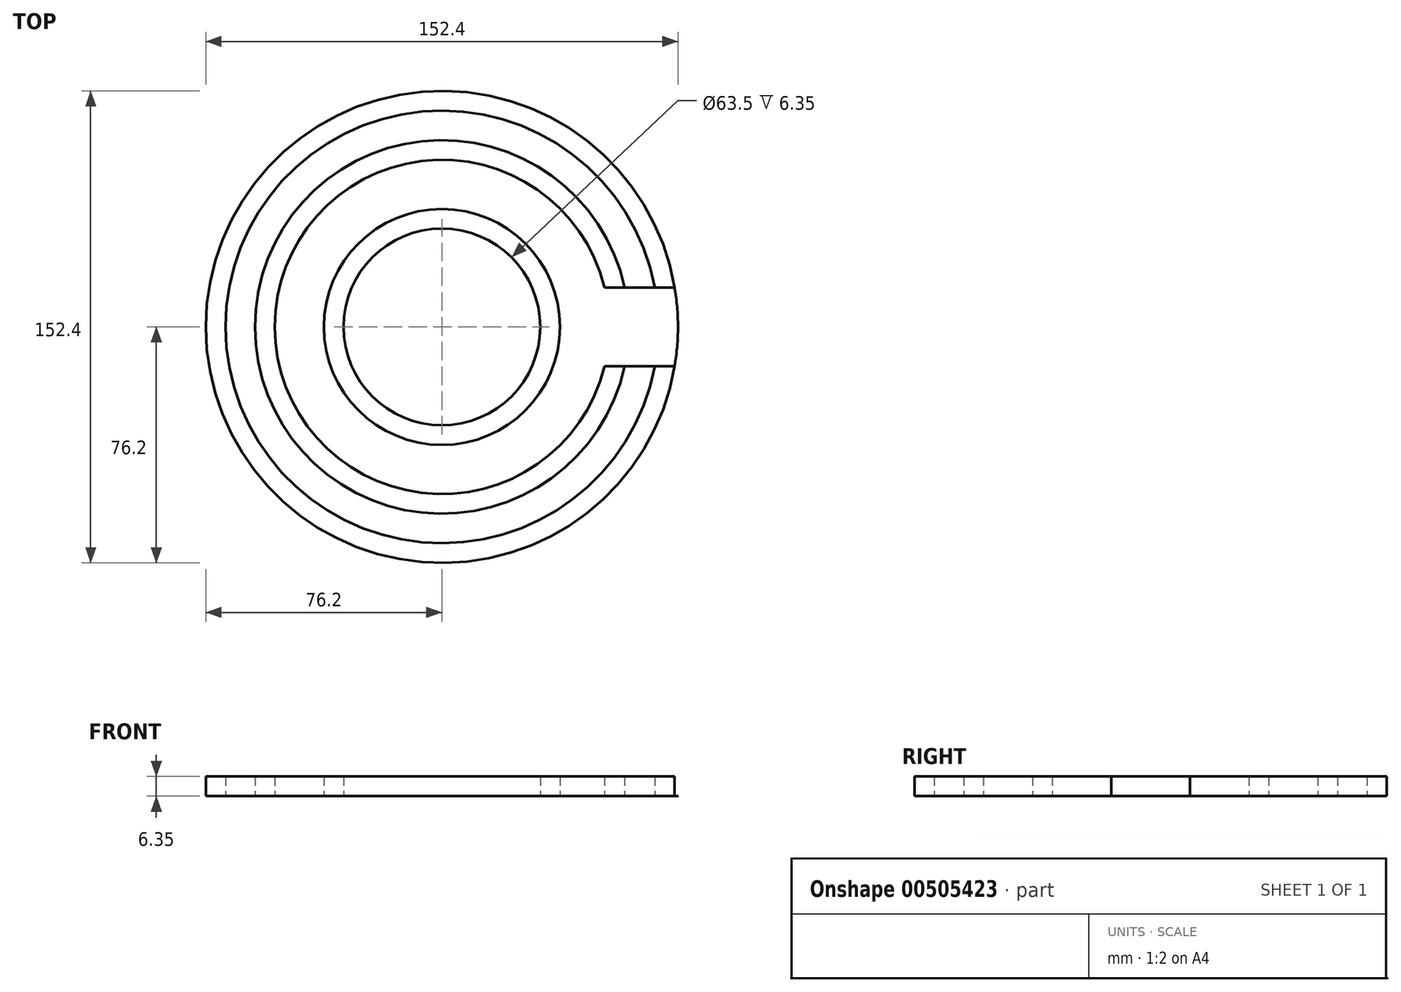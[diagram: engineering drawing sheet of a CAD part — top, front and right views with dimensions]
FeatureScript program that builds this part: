
annotation { "Feature Type Name" : "Feature", "Feature Type Description" : "" }
export const myFeature = defineFeature(function(context is Context, id is Id, definition is map)
    precondition{}
    {
        {
            var Q0;
            Q0=qCreatedBy(makeId("Top.planeOp"),FACE);
            var sketch = newSketch(context, id + "F0", { "sketchPlane" : qUnion([Q0])});
            skCircle(sketch, "E0", {"center": v(0, 0) * mm, "radius": 76.2 * mm});
            skCircle(sketch, "E1", {"center": v(0, 0) * mm, "radius": 69.85 * mm});
            skCircle(sketch, "E2", {"center": v(0, 0) * mm, "radius": 60.33 * mm});
            skCircle(sketch, "E3", {"center": v(0, 0) * mm, "radius": 53.98 * mm});
            skCircle(sketch, "E4", {"center": v(0, 0) * mm, "radius": 38.1 * mm});
            skCircle(sketch, "E5", {"center": v(0, 0) * mm, "radius": 31.75 * mm});
            skLineSegment(sketch, "E6", {"start": v(48.66, 12.7) * mm, "end": v(80.06, 12.7) * mm});
            skLineSegment(sketch, "E7", {"start": v(48.66, -12.7) * mm, "end": v(80.06, -12.7) * mm});
            skSolve(sketch);
        }
        {
            var Q0;
            {var subQ0=sQuery(id+"F0.wireOp",EDGE,"E6");var subQ1=sQuery(id+"F0.wireOp",EDGE,"E1");var subQ2=makeQuery(id+"F0.imprint","INTERSECT",VERTEX,{"derivedFrom":[subQ1,subQ0]});Q0=makeQuery(id+"F0.imprint","IMPRINT",FACE,{"disambiguationData":[TD([[makeQuery(id+"F0.imprint","IMPRINT",EDGE,{"disambiguationData":[TD([[subQ2,-1.0]])],"derivedFrom":subQ1}),1.0]])]});}
            var Q1;
            Q1=makeQuery(id+"F0.imprint","IMPRINT",FACE,{"disambiguationData":[TD([[makeQuery(id+"F0.imprint","IMPRINT",EDGE,{"derivedFrom":sQuery(id+"F0.wireOp",EDGE,"E5")}),1.0]])]});
            extrude(context, id + "F1", {"entities" : qUnion([Q0, Q1]), "depth" : 6.35 * mm});
        }
        {
            var Q0;
            Q0=qCreatedBy(makeId("Top.planeOp"),FACE);
            var sketch = newSketch(context, id + "F2", { "sketchPlane" : qUnion([Q0])});
            skCircle(sketch, "E8", {"center": v(0, 0) * mm, "radius": 76.2 * mm});
            skCircle(sketch, "E9", {"center": v(0, 0) * mm, "radius": 69.85 * mm});
            skCircle(sketch, "E10", {"center": v(0, 0) * mm, "radius": 60.33 * mm});
            skCircle(sketch, "E11", {"center": v(0, 0) * mm, "radius": 53.98 * mm});
            skCircle(sketch, "E12", {"center": v(0, 0) * mm, "radius": 38.1 * mm});
            skCircle(sketch, "E13", {"center": v(0, 0) * mm, "radius": 31.75 * mm});
            skLineSegment(sketch, "E14", {"start": v(48.66, 12.7) * mm, "end": v(80.06, 12.7) * mm});
            skLineSegment(sketch, "E15", {"start": v(48.66, -12.7) * mm, "end": v(80.06, -12.7) * mm});
            skSolve(sketch);
        }
        {
            var Q0;
            Q0=makeQuery(id+"F2.imprint","IMPRINT",FACE,{"disambiguationData":[TD([[makeQuery(id+"F2.imprint","IMPRINT",EDGE,{"derivedFrom":sQuery(id+"F2.wireOp",EDGE,"E12")}),1.0]])]});
            var Q1;
            {var subQ0=sQuery(id+"F2.wireOp",EDGE,"E14");var subQ1=sQuery(id+"F2.wireOp",EDGE,"E10");var subQ2=makeQuery(id+"F2.imprint","INTERSECT",VERTEX,{"derivedFrom":[subQ1,subQ0]});Q1=makeQuery(id+"F2.imprint","IMPRINT",FACE,{"disambiguationData":[TD([[makeQuery(id+"F2.imprint","IMPRINT",EDGE,{"disambiguationData":[TD([[subQ2,-1.0]])],"derivedFrom":subQ1}),1.0]])]});}
            var Q2;
            {var subQ0=sQuery(id+"F2.wireOp",EDGE,"E14");var subQ1=sQuery(id+"F2.wireOp",EDGE,"E8");var subQ2=makeQuery(id+"F2.imprint","INTERSECT",VERTEX,{"derivedFrom":[subQ1,subQ0]});Q2=makeQuery(id+"F2.imprint","IMPRINT",FACE,{"disambiguationData":[TD([[makeQuery(id+"F2.imprint","IMPRINT",EDGE,{"disambiguationData":[TD([[subQ2,-1.0]])],"derivedFrom":subQ1}),1.0]])]});}
            extrude(context, id + "F3", {"entities" : qUnion([Q0, Q1, Q2]), "depth" : 6.35 * mm});
        }
        {
            var Q0;
            Q0=qCreatedBy(makeId("Top.planeOp"),FACE);
            var sketch = newSketch(context, id + "F4", { "sketchPlane" : qUnion([Q0])});
            skCircle(sketch, "E16", {"center": v(0, 0) * mm, "radius": 76.2 * mm});
            skSolve(sketch);
        }
        {
            var Q0;
            Q0=makeQuery(id+"F4.imprint","IMPRINT",FACE,{"disambiguationData":[TD([[makeQuery(id+"F4.imprint","IMPRINT",EDGE,{"derivedFrom":sQuery(id+"F4.wireOp",EDGE,"E16")}),1.0]])]});
            extrude(context, id + "F5", {"entities" : qUnion([Q0]), "depth" : 0.03 * mm});
        }
    });
